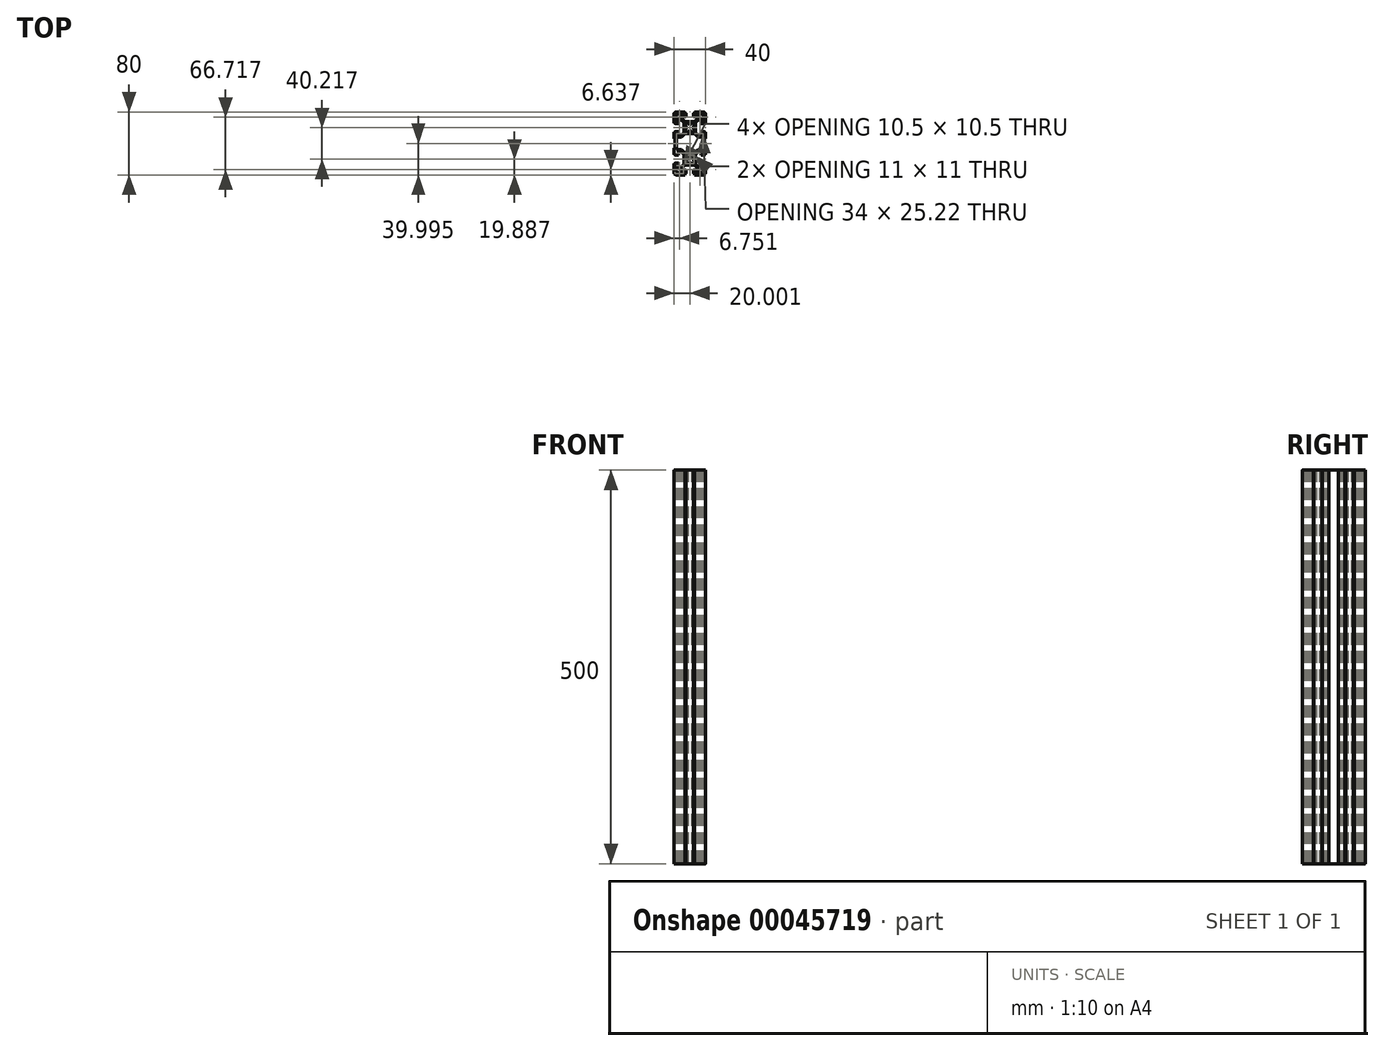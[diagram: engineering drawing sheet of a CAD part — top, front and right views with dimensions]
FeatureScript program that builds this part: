
annotation { "Feature Type Name" : "Feature", "Feature Type Description" : "" }
export const myFeature = defineFeature(function(context is Context, id is Id, definition is map)
    precondition{}
    {
        {
            var Q0;
            Q0=qCreatedBy(makeId("Top.planeOp"),FACE);
            var sketch = newSketch(context, id + "F0", { "sketchPlane" : qUnion([Q0])});
            skLineSegment(sketch, "E0", {"start": v(-19.67, 37.28) * mm, "end": v(-19.67, 26.18) * mm});
            skLineSegment(sketch, "E1", {"start": v(-19.67, 26.18) * mm, "end": v(-18.17, 26.18) * mm});
            skLineSegment(sketch, "E2", {"start": v(-18.17, 26.18) * mm, "end": v(-18.17, 25.38) * mm});
            skLineSegment(sketch, "E3", {"start": v(-18.17, 25.38) * mm, "end": v(-13.67, 25.38) * mm});
            skLineSegment(sketch, "E4", {"start": v(-13.67, 25.38) * mm, "end": v(-13.67, 30.43) * mm});
            skLineSegment(sketch, "E5", {"start": v(-13.67, 30.43) * mm, "end": v(-11.13, 30.43) * mm});
            skLineSegment(sketch, "E6", {"start": v(-11.13, 30.43) * mm, "end": v(-7.17, 26.47) * mm});
            skLineSegment(sketch, "E7", {"start": v(-7.17, 26.47) * mm, "end": v(-7.17, 14.3) * mm});
            skLineSegment(sketch, "E8", {"start": v(-7.17, 14.3) * mm, "end": v(-11.13, 10.33) * mm});
            skLineSegment(sketch, "E9", {"start": v(-11.13, 10.33) * mm, "end": v(-13.67, 10.33) * mm});
            skLineSegment(sketch, "E10", {"start": v(-13.67, 10.33) * mm, "end": v(-13.67, 15.38) * mm});
            skLineSegment(sketch, "E11", {"start": v(-13.67, 15.38) * mm, "end": v(-18.17, 15.38) * mm});
            skLineSegment(sketch, "E12", {"start": v(-18.17, 15.38) * mm, "end": v(-18.17, 14.58) * mm});
            skLineSegment(sketch, "E13", {"start": v(-18.17, 14.58) * mm, "end": v(-19.67, 14.58) * mm});
            skLineSegment(sketch, "E14", {"start": v(-19.67, 14.58) * mm, "end": v(-19.67, 6.38) * mm});
            skLineSegment(sketch, "E15", {"start": v(-19.67, 6.38) * mm, "end": v(-18.67, 6.38) * mm});
            skLineSegment(sketch, "E16", {"start": v(-18.67, 6.38) * mm, "end": v(-18.67, -5.83) * mm});
            skLineSegment(sketch, "E17", {"start": v(-18.67, -5.83) * mm, "end": v(-19.67, -5.83) * mm});
            skLineSegment(sketch, "E18", {"start": v(-19.67, -5.83) * mm, "end": v(-19.67, -14.03) * mm});
            skLineSegment(sketch, "E19", {"start": v(-19.67, -14.03) * mm, "end": v(-18.17, -14.03) * mm});
            skLineSegment(sketch, "E20", {"start": v(-18.17, -14.03) * mm, "end": v(-18.17, -14.83) * mm});
            skLineSegment(sketch, "E21", {"start": v(-18.17, -14.83) * mm, "end": v(-13.67, -14.83) * mm});
            skLineSegment(sketch, "E22", {"start": v(-13.67, -14.83) * mm, "end": v(-13.67, -9.78) * mm});
            skLineSegment(sketch, "E23", {"start": v(-13.67, -9.78) * mm, "end": v(-11.13, -9.78) * mm});
            skLineSegment(sketch, "E24", {"start": v(-11.13, -9.78) * mm, "end": v(-7.17, -13.75) * mm});
            skLineSegment(sketch, "E25", {"start": v(-7.17, -13.75) * mm, "end": v(-7.17, -25.92) * mm});
            skLineSegment(sketch, "E26", {"start": v(-7.17, -25.92) * mm, "end": v(-11.13, -29.88) * mm});
            skLineSegment(sketch, "E27", {"start": v(-11.13, -29.88) * mm, "end": v(-13.67, -29.88) * mm});
            skLineSegment(sketch, "E28", {"start": v(-13.67, -29.88) * mm, "end": v(-13.67, -24.83) * mm});
            skLineSegment(sketch, "E29", {"start": v(-13.67, -24.83) * mm, "end": v(-18.17, -24.83) * mm});
            skLineSegment(sketch, "E30", {"start": v(-18.17, -24.83) * mm, "end": v(-18.17, -25.63) * mm});
            skLineSegment(sketch, "E31", {"start": v(-18.17, -25.63) * mm, "end": v(-19.67, -25.63) * mm});
            skLineSegment(sketch, "E32", {"start": v(-19.67, -25.63) * mm, "end": v(-19.67, -36.72) * mm});
            skLineSegment(sketch, "E33", {"start": v(-16.67, -39.72) * mm, "end": v(-5.47, -39.72) * mm});
            skLineSegment(sketch, "E34", {"start": v(-5.47, -39.72) * mm, "end": v(-5.47, -38.22) * mm});
            skLineSegment(sketch, "E35", {"start": v(-5.47, -38.22) * mm, "end": v(-4.67, -38.22) * mm});
            skLineSegment(sketch, "E36", {"start": v(-4.67, -38.22) * mm, "end": v(-4.67, -33.72) * mm});
            skLineSegment(sketch, "E37", {"start": v(-4.67, -33.72) * mm, "end": v(-9.72, -33.72) * mm});
            skLineSegment(sketch, "E38", {"start": v(-9.72, -33.72) * mm, "end": v(-9.72, -31.19) * mm});
            skLineSegment(sketch, "E39", {"start": v(-9.72, -31.19) * mm, "end": v(-5.75, -27.22) * mm});
            skLineSegment(sketch, "E40", {"start": v(-5.75, -27.22) * mm, "end": v(6.42, -27.22) * mm});
            skLineSegment(sketch, "E41", {"start": v(6.42, -27.22) * mm, "end": v(10.38, -31.19) * mm});
            skLineSegment(sketch, "E42", {"start": v(10.38, -31.19) * mm, "end": v(10.38, -33.72) * mm});
            skLineSegment(sketch, "E43", {"start": v(10.38, -33.72) * mm, "end": v(5.33, -33.72) * mm});
            skLineSegment(sketch, "E44", {"start": v(5.33, -33.72) * mm, "end": v(5.33, -38.22) * mm});
            skLineSegment(sketch, "E45", {"start": v(5.33, -38.22) * mm, "end": v(6.13, -38.22) * mm});
            skLineSegment(sketch, "E46", {"start": v(6.13, -38.22) * mm, "end": v(6.13, -39.72) * mm});
            skLineSegment(sketch, "E47", {"start": v(6.13, -39.72) * mm, "end": v(17.33, -39.72) * mm});
            skLineSegment(sketch, "E48", {"start": v(20.33, -36.72) * mm, "end": v(20.33, -25.63) * mm});
            skLineSegment(sketch, "E49", {"start": v(20.33, -25.63) * mm, "end": v(18.83, -25.63) * mm});
            skLineSegment(sketch, "E50", {"start": v(18.83, -25.63) * mm, "end": v(18.83, -24.83) * mm});
            skLineSegment(sketch, "E51", {"start": v(18.83, -24.83) * mm, "end": v(14.33, -24.83) * mm});
            skLineSegment(sketch, "E52", {"start": v(14.33, -24.83) * mm, "end": v(14.33, -29.88) * mm});
            skLineSegment(sketch, "E53", {"start": v(14.33, -29.88) * mm, "end": v(11.8, -29.88) * mm});
            skLineSegment(sketch, "E54", {"start": v(11.8, -29.88) * mm, "end": v(7.83, -25.92) * mm});
            skLineSegment(sketch, "E55", {"start": v(7.83, -25.92) * mm, "end": v(7.83, -13.75) * mm});
            skLineSegment(sketch, "E56", {"start": v(7.83, -13.75) * mm, "end": v(11.8, -9.78) * mm});
            skLineSegment(sketch, "E57", {"start": v(11.8, -9.78) * mm, "end": v(14.33, -9.78) * mm});
            skLineSegment(sketch, "E58", {"start": v(14.33, -9.78) * mm, "end": v(14.33, -14.83) * mm});
            skLineSegment(sketch, "E59", {"start": v(14.33, -14.83) * mm, "end": v(18.83, -14.83) * mm});
            skLineSegment(sketch, "E60", {"start": v(18.83, -14.83) * mm, "end": v(18.83, -14.03) * mm});
            skLineSegment(sketch, "E61", {"start": v(18.83, -14.03) * mm, "end": v(20.33, -14.03) * mm});
            skLineSegment(sketch, "E62", {"start": v(20.33, -14.03) * mm, "end": v(20.33, -5.83) * mm});
            skLineSegment(sketch, "E63", {"start": v(20.33, -5.83) * mm, "end": v(19.33, -5.83) * mm});
            skLineSegment(sketch, "E64", {"start": v(19.33, -5.83) * mm, "end": v(19.33, 6.38) * mm});
            skLineSegment(sketch, "E65", {"start": v(19.33, 6.38) * mm, "end": v(20.33, 6.38) * mm});
            skLineSegment(sketch, "E66", {"start": v(20.33, 6.38) * mm, "end": v(20.33, 14.58) * mm});
            skLineSegment(sketch, "E67", {"start": v(20.33, 14.58) * mm, "end": v(18.83, 14.58) * mm});
            skLineSegment(sketch, "E68", {"start": v(18.83, 14.58) * mm, "end": v(18.83, 15.38) * mm});
            skLineSegment(sketch, "E69", {"start": v(18.83, 15.38) * mm, "end": v(14.33, 15.38) * mm});
            skLineSegment(sketch, "E70", {"start": v(14.33, 15.38) * mm, "end": v(14.33, 10.33) * mm});
            skLineSegment(sketch, "E71", {"start": v(14.33, 10.33) * mm, "end": v(11.8, 10.33) * mm});
            skLineSegment(sketch, "E72", {"start": v(11.8, 10.33) * mm, "end": v(7.83, 14.3) * mm});
            skLineSegment(sketch, "E73", {"start": v(7.83, 14.3) * mm, "end": v(7.83, 26.47) * mm});
            skLineSegment(sketch, "E74", {"start": v(7.83, 26.47) * mm, "end": v(11.8, 30.43) * mm});
            skLineSegment(sketch, "E75", {"start": v(11.8, 30.43) * mm, "end": v(14.33, 30.43) * mm});
            skLineSegment(sketch, "E76", {"start": v(14.33, 30.43) * mm, "end": v(14.33, 25.38) * mm});
            skLineSegment(sketch, "E77", {"start": v(14.33, 25.38) * mm, "end": v(18.83, 25.38) * mm});
            skLineSegment(sketch, "E78", {"start": v(18.83, 25.38) * mm, "end": v(18.83, 26.18) * mm});
            skLineSegment(sketch, "E79", {"start": v(18.83, 26.18) * mm, "end": v(20.33, 26.18) * mm});
            skLineSegment(sketch, "E80", {"start": v(20.33, 26.18) * mm, "end": v(20.33, 37.28) * mm});
            skLineSegment(sketch, "E81", {"start": v(17.33, 40.28) * mm, "end": v(6.13, 40.28) * mm});
            skLineSegment(sketch, "E82", {"start": v(6.13, 40.28) * mm, "end": v(6.13, 38.78) * mm});
            skLineSegment(sketch, "E83", {"start": v(6.13, 38.78) * mm, "end": v(5.33, 38.78) * mm});
            skLineSegment(sketch, "E84", {"start": v(5.33, 38.78) * mm, "end": v(5.33, 34.28) * mm});
            skLineSegment(sketch, "E85", {"start": v(5.33, 34.28) * mm, "end": v(10.38, 34.28) * mm});
            skLineSegment(sketch, "E86", {"start": v(10.38, 34.28) * mm, "end": v(10.38, 31.74) * mm});
            skLineSegment(sketch, "E87", {"start": v(10.38, 31.74) * mm, "end": v(6.42, 27.78) * mm});
            skLineSegment(sketch, "E88", {"start": v(6.42, 27.78) * mm, "end": v(-5.75, 27.78) * mm});
            skLineSegment(sketch, "E89", {"start": v(-5.75, 27.78) * mm, "end": v(-9.72, 31.74) * mm});
            skLineSegment(sketch, "E90", {"start": v(-9.72, 31.74) * mm, "end": v(-9.72, 34.28) * mm});
            skLineSegment(sketch, "E91", {"start": v(-9.72, 34.28) * mm, "end": v(-4.67, 34.28) * mm});
            skLineSegment(sketch, "E92", {"start": v(-4.67, 34.28) * mm, "end": v(-4.67, 38.78) * mm});
            skLineSegment(sketch, "E93", {"start": v(-4.67, 38.78) * mm, "end": v(-5.47, 38.78) * mm});
            skLineSegment(sketch, "E94", {"start": v(-5.47, 38.78) * mm, "end": v(-5.47, 40.28) * mm});
            skLineSegment(sketch, "E95", {"start": v(-5.47, 40.28) * mm, "end": v(-16.67, 40.28) * mm});
            skLineSegment(sketch, "E96", {"start": v(-14.17, 37.63) * mm, "end": v(-14.17, 38.88) * mm});
            skLineSegment(sketch, "E97", {"start": v(-14.17, 38.88) * mm, "end": v(-9.17, 38.88) * mm});
            skLineSegment(sketch, "E98", {"start": v(-9.17, 35.88) * mm, "end": v(-11.42, 35.88) * mm});
            skLineSegment(sketch, "E99", {"start": v(-15.17, 32.13) * mm, "end": v(-15.17, 29.88) * mm});
            skLineSegment(sketch, "E100", {"start": v(-16.92, 34.88) * mm, "end": v(-18.17, 34.88) * mm});
            skLineSegment(sketch, "E101", {"start": v(-18.17, 34.88) * mm, "end": v(-18.17, 29.88) * mm});
            skArc(sketch, "E102", {"start": v(-9.17, 35.88) * mm, "mid": v(-7.67, 37.38) * mm, "end": v(-9.17, 38.88) * mm});
            skArc(sketch, "E103", {"start": v(-18.17, 29.88) * mm, "mid": v(-16.67, 28.38) * mm, "end": v(-15.17, 29.88) * mm});
            skArc(sketch, "E104", {"start": v(-14.17, 37.63) * mm, "mid": v(-16.11, 36.83) * mm, "end": v(-16.92, 34.88) * mm});
            skArc(sketch, "E105", {"start": v(9.83, 38.88) * mm, "mid": v(8.33, 37.38) * mm, "end": v(9.83, 35.88) * mm});
            skArc(sketch, "E106", {"start": v(15.83, 29.88) * mm, "mid": v(17.33, 28.38) * mm, "end": v(18.83, 29.88) * mm});
            skArc(sketch, "E107", {"start": v(-4.25, 22.38) * mm, "mid": v(-4.67, 20.38) * mm, "end": v(-4.25, 18.39) * mm});
            skArc(sketch, "E108", {"start": v(-11.6, -35.33) * mm, "mid": v(-12.22, -32.39) * mm, "end": v(-15.17, -31.77) * mm});
            skArc(sketch, "E109", {"start": v(14.83, -37.08) * mm, "mid": v(16.78, -36.28) * mm, "end": v(17.58, -34.33) * mm});
            skArc(sketch, "E110", {"start": v(9.83, -35.33) * mm, "mid": v(8.33, -36.83) * mm, "end": v(9.83, -38.33) * mm});
            skArc(sketch, "E111", {"start": v(18.83, -29.33) * mm, "mid": v(17.33, -27.83) * mm, "end": v(15.83, -29.33) * mm});
            skArc(sketch, "E112", {"start": v(12.27, 35.88) * mm, "mid": v(12.89, 32.94) * mm, "end": v(15.83, 32.32) * mm});
            skLineSegment(sketch, "E113", {"start": v(-15.17, 32.13) * mm, "end": v(-15.17, 32.32) * mm});
            skLineSegment(sketch, "E114", {"start": v(-11.42, 35.88) * mm, "end": v(-11.6, 35.88) * mm});
            skLineSegment(sketch, "E115", {"start": v(9.83, 38.88) * mm, "end": v(14.83, 38.88) * mm});
            skLineSegment(sketch, "E116", {"start": v(14.83, 38.88) * mm, "end": v(14.83, 37.63) * mm});
            skLineSegment(sketch, "E117", {"start": v(9.83, 35.88) * mm, "end": v(12.27, 35.88) * mm});
            skLineSegment(sketch, "E118", {"start": v(17.58, 34.88) * mm, "end": v(18.83, 34.88) * mm});
            skLineSegment(sketch, "E119", {"start": v(18.83, 34.88) * mm, "end": v(18.83, 29.88) * mm});
            skLineSegment(sketch, "E120", {"start": v(15.83, 29.88) * mm, "end": v(15.83, 32.32) * mm});
            skArc(sketch, "E121.trimOffspring", {"start": v(17.58, 34.88) * mm, "mid": v(16.78, 36.83) * mm, "end": v(14.83, 37.63) * mm});
            skArc(sketch, "E122.trimOffspring", {"start": v(-15.17, 32.32) * mm, "mid": v(-12.22, 32.94) * mm, "end": v(-11.6, 35.88) * mm});
            skLineSegment(sketch, "E123", {"start": v(-4.25, 22.38) * mm, "end": v(-5.17, 22.78) * mm});
            skLineSegment(sketch, "E124", {"start": v(-5.17, 22.78) * mm, "end": v(-5.17, 25.88) * mm});
            skLineSegment(sketch, "E125", {"start": v(-5.17, 25.88) * mm, "end": v(-2.07, 25.88) * mm});
            skLineSegment(sketch, "E126", {"start": v(-2.07, 25.88) * mm, "end": v(-1.67, 24.97) * mm});
            skLineSegment(sketch, "E127", {"start": v(2.33, 24.97) * mm, "end": v(2.73, 25.88) * mm});
            skLineSegment(sketch, "E128", {"start": v(2.73, 25.88) * mm, "end": v(5.83, 25.88) * mm});
            skLineSegment(sketch, "E129", {"start": v(5.83, 25.88) * mm, "end": v(5.83, 22.78) * mm});
            skLineSegment(sketch, "E130", {"start": v(-4.25, 18.39) * mm, "end": v(-5.17, 17.99) * mm});
            skLineSegment(sketch, "E131", {"start": v(-5.17, 17.99) * mm, "end": v(-5.17, 14.88) * mm});
            skLineSegment(sketch, "E132", {"start": v(-5.17, 14.88) * mm, "end": v(-2.07, 14.88) * mm});
            skLineSegment(sketch, "E133", {"start": v(-2.07, 14.88) * mm, "end": v(-1.67, 15.8) * mm});
            skLineSegment(sketch, "E134", {"start": v(2.33, 15.8) * mm, "end": v(2.73, 14.88) * mm});
            skLineSegment(sketch, "E135", {"start": v(2.73, 14.88) * mm, "end": v(5.83, 14.88) * mm});
            skLineSegment(sketch, "E136", {"start": v(5.83, 14.88) * mm, "end": v(5.83, 17.99) * mm});
            skArc(sketch, "E137.trimOffspring", {"start": v(2.33, 24.97) * mm, "mid": v(0.33, 25.38) * mm, "end": v(-1.67, 24.97) * mm});
            skArc(sketch, "E138.trimOffspring", {"start": v(4.91, 18.39) * mm, "mid": v(5.33, 20.38) * mm, "end": v(4.91, 22.38) * mm});
            skLineSegment(sketch, "E139", {"start": v(-16.67, 8.33) * mm, "end": v(-16.67, -7.78) * mm});
            skLineSegment(sketch, "E140", {"start": v(-16.67, -7.78) * mm, "end": v(-10.3, -7.78) * mm});
            skLineSegment(sketch, "E141", {"start": v(-10.3, -7.78) * mm, "end": v(-5.75, -12.33) * mm});
            skLineSegment(sketch, "E142", {"start": v(-5.75, -12.33) * mm, "end": v(6.42, -12.33) * mm});
            skLineSegment(sketch, "E143", {"start": v(6.42, -12.33) * mm, "end": v(10.97, -7.78) * mm});
            skLineSegment(sketch, "E144", {"start": v(10.97, -7.78) * mm, "end": v(17.33, -7.78) * mm});
            skLineSegment(sketch, "E145", {"start": v(17.33, -7.78) * mm, "end": v(17.33, 8.33) * mm});
            skLineSegment(sketch, "E146", {"start": v(17.33, 8.33) * mm, "end": v(10.97, 8.33) * mm});
            skLineSegment(sketch, "E147", {"start": v(10.97, 8.33) * mm, "end": v(6.42, 12.88) * mm});
            skLineSegment(sketch, "E148", {"start": v(6.42, 12.88) * mm, "end": v(-5.75, 12.88) * mm});
            skLineSegment(sketch, "E149", {"start": v(-5.75, 12.88) * mm, "end": v(-10.3, 8.33) * mm});
            skLineSegment(sketch, "E150", {"start": v(-10.3, 8.33) * mm, "end": v(-16.67, 8.33) * mm});
            skLineSegment(sketch, "E151", {"start": v(-1.67, -15.25) * mm, "end": v(-2.07, -14.33) * mm});
            skLineSegment(sketch, "E152", {"start": v(-2.07, -14.33) * mm, "end": v(-5.17, -14.33) * mm});
            skLineSegment(sketch, "E153", {"start": v(-5.17, -14.33) * mm, "end": v(-5.17, -17.44) * mm});
            skLineSegment(sketch, "E154", {"start": v(-5.17, -17.44) * mm, "end": v(-4.25, -17.84) * mm});
            skLineSegment(sketch, "E155", {"start": v(2.33, -15.25) * mm, "end": v(2.73, -14.33) * mm});
            skLineSegment(sketch, "E156", {"start": v(2.73, -14.33) * mm, "end": v(5.83, -14.33) * mm});
            skLineSegment(sketch, "E157", {"start": v(5.83, -14.33) * mm, "end": v(5.83, -17.44) * mm});
            skLineSegment(sketch, "E158", {"start": v(5.83, -17.44) * mm, "end": v(4.91, -17.84) * mm});
            skLineSegment(sketch, "E159", {"start": v(-4.25, -21.83) * mm, "end": v(-5.17, -22.23) * mm});
            skLineSegment(sketch, "E160", {"start": v(-5.17, -22.23) * mm, "end": v(-5.17, -25.33) * mm});
            skLineSegment(sketch, "E161", {"start": v(-5.17, -25.33) * mm, "end": v(-2.07, -25.33) * mm});
            skLineSegment(sketch, "E162", {"start": v(-2.07, -25.33) * mm, "end": v(-1.67, -24.42) * mm});
            skLineSegment(sketch, "E163", {"start": v(2.33, -24.42) * mm, "end": v(2.73, -25.33) * mm});
            skLineSegment(sketch, "E164", {"start": v(2.73, -25.33) * mm, "end": v(5.83, -25.33) * mm});
            skLineSegment(sketch, "E165", {"start": v(5.83, -25.33) * mm, "end": v(5.83, -22.23) * mm});
            skLineSegment(sketch, "E166", {"start": v(5.83, -22.23) * mm, "end": v(4.91, -21.83) * mm});
            skLineSegment(sketch, "E167", {"start": v(-18.17, -29.33) * mm, "end": v(-18.17, -34.33) * mm});
            skLineSegment(sketch, "E168", {"start": v(-18.17, -34.33) * mm, "end": v(-16.92, -34.33) * mm});
            skLineSegment(sketch, "E169", {"start": v(-15.17, -29.33) * mm, "end": v(-15.17, -31.77) * mm});
            skLineSegment(sketch, "E170", {"start": v(-11.42, -34.33) * mm, "end": v(-11.42, -35.33) * mm});
            skLineSegment(sketch, "E171", {"start": v(-9.17, -35.33) * mm, "end": v(-11.6, -35.33) * mm});
            skLineSegment(sketch, "E172", {"start": v(-14.17, -37.08) * mm, "end": v(-14.17, -38.33) * mm});
            skLineSegment(sketch, "E173", {"start": v(-14.17, -38.33) * mm, "end": v(-9.17, -38.33) * mm});
            skLineSegment(sketch, "E174", {"start": v(9.83, -35.33) * mm, "end": v(12.27, -35.33) * mm});
            skLineSegment(sketch, "E175", {"start": v(9.83, -38.33) * mm, "end": v(14.83, -38.33) * mm});
            skLineSegment(sketch, "E176", {"start": v(14.83, -38.33) * mm, "end": v(14.83, -37.08) * mm});
            skLineSegment(sketch, "E177", {"start": v(17.58, -34.33) * mm, "end": v(18.83, -34.33) * mm});
            skLineSegment(sketch, "E178", {"start": v(18.83, -34.33) * mm, "end": v(18.83, -29.33) * mm});
            skLineSegment(sketch, "E179", {"start": v(15.83, -29.33) * mm, "end": v(15.83, -31.77) * mm});
            skArc(sketch, "E180.trimOffspring", {"start": v(15.83, -31.77) * mm, "mid": v(12.89, -32.39) * mm, "end": v(12.27, -35.33) * mm});
            skLineSegment(sketch, "E181", {"start": v(4.91, 18.39) * mm, "end": v(5.83, 17.99) * mm});
            skLineSegment(sketch, "E182", {"start": v(4.91, 22.38) * mm, "end": v(5.83, 22.78) * mm});
            skPoint(sketch, "E183.center.orphan", {"position": v(0.33, -19.83) * mm});
            skPoint(sketch, "E184.center.orphan", {"position": v(-16.67, -29.33) * mm});
            skPoint(sketch, "E185.center.orphan", {"position": v(-9.17, -36.83) * mm});
            skArc(sketch, "E186", {"start": v(-19.67, -36.72) * mm, "mid": v(-18.8, -38.85) * mm, "end": v(-16.67, -39.72) * mm});
            skArc(sketch, "E187", {"start": v(17.33, -39.72) * mm, "mid": v(19.45, -38.85) * mm, "end": v(20.33, -36.72) * mm});
            skArc(sketch, "E188", {"start": v(20.33, 37.28) * mm, "mid": v(19.45, 39.4) * mm, "end": v(17.33, 40.28) * mm});
            skArc(sketch, "E189", {"start": v(-19.67, 37.28) * mm, "mid": v(-18.8, 39.4) * mm, "end": v(-16.67, 40.28) * mm});
            skArc(sketch, "E190", {"start": v(-1.67, 15.8) * mm, "mid": v(0.33, 15.38) * mm, "end": v(2.33, 15.8) * mm});
            skArc(sketch, "E191", {"start": v(-4.25, -17.84) * mm, "mid": v(-4.67, -19.83) * mm, "end": v(-4.25, -21.83) * mm});
            skArc(sketch, "E192", {"start": v(-1.67, -15.25) * mm, "mid": v(0.33, -14.83) * mm, "end": v(2.33, -15.25) * mm});
            skArc(sketch, "E193", {"start": v(4.91, -17.84) * mm, "mid": v(5.33, -19.83) * mm, "end": v(4.91, -21.83) * mm});
            skArc(sketch, "E194", {"start": v(2.33, -24.42) * mm, "mid": v(0.33, -24.83) * mm, "end": v(-1.67, -24.42) * mm});
            skArc(sketch, "E195", {"start": v(-18.17, -29.33) * mm, "mid": v(-16.67, -27.83) * mm, "end": v(-15.17, -29.33) * mm});
            skArc(sketch, "E196", {"start": v(-9.17, -35.33) * mm, "mid": v(-7.67, -36.83) * mm, "end": v(-9.17, -38.33) * mm});
            skArc(sketch, "E197", {"start": v(-16.92, -34.33) * mm, "mid": v(-16.11, -36.28) * mm, "end": v(-14.17, -37.08) * mm});
            skSolve(sketch);
        }
        {
            var Q0;
            Q0 = qSketchRegion(id + "F0", true);
            extrude(context, id + "F1", {"entities" : qUnion([Q0]), "depth" : 500 * mm});
        }
    });
